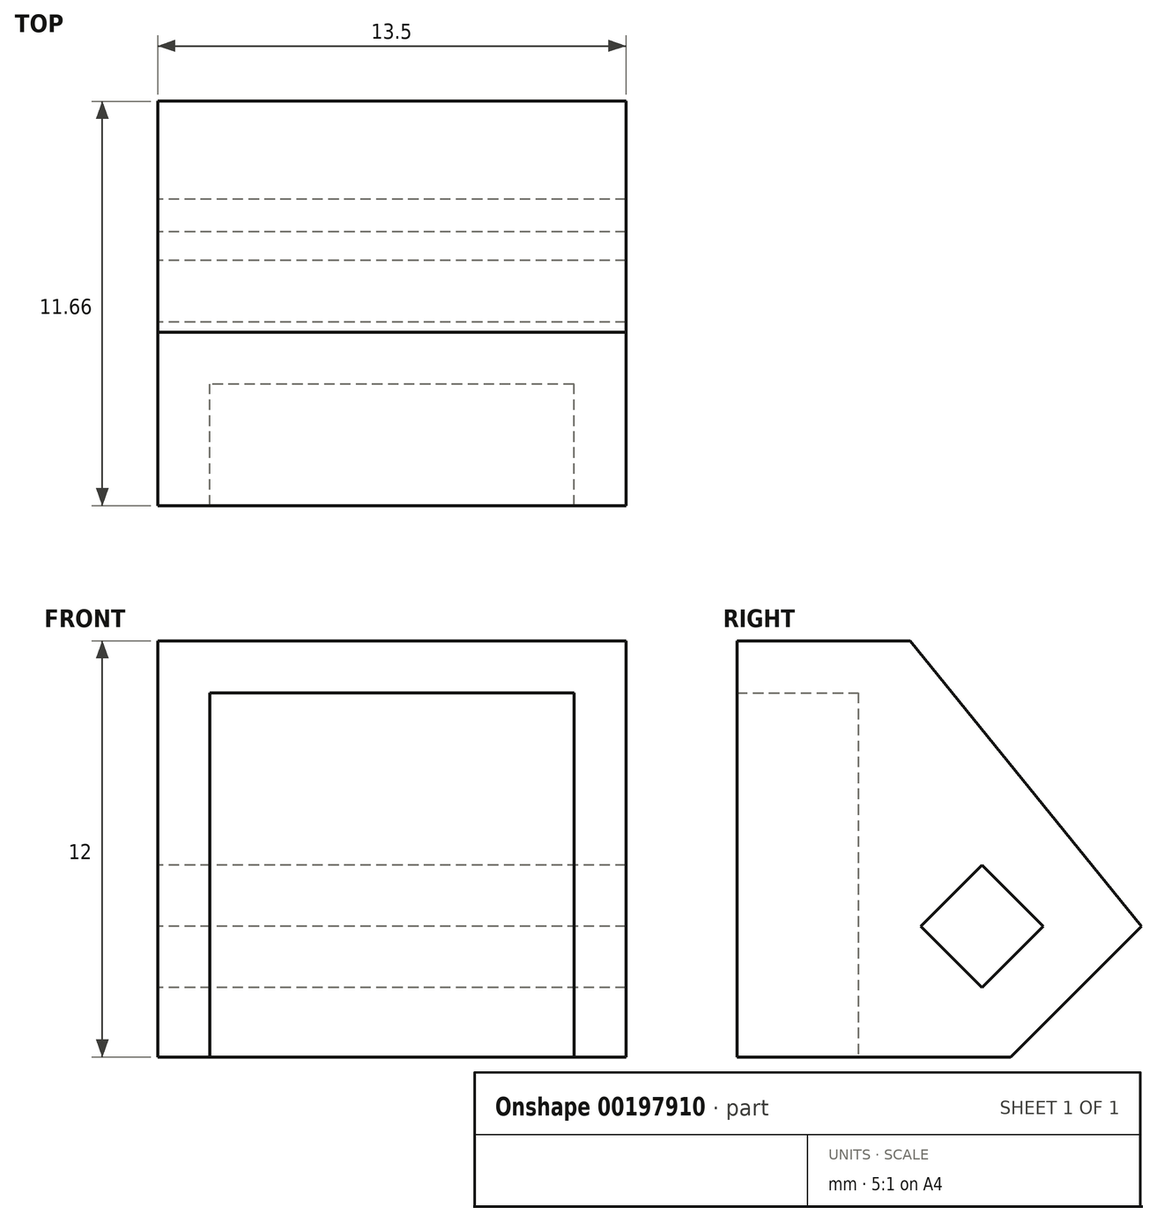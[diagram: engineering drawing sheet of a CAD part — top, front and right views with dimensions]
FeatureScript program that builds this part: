
annotation { "Feature Type Name" : "Feature", "Feature Type Description" : "" }
export const myFeature = defineFeature(function(context is Context, id is Id, definition is map)
    precondition{}
    {
        {
            var Q0;
            Q0=qCreatedBy(makeId("Front.planeOp"),FACE);
            var sketch = newSketch(context, id + "F0", { "sketchPlane" : qUnion([Q0])});
            skLineSegment(sketch, "E0.bottom", {"start": v(5.25, 5.25) * mm, "end": v(-5.25, 5.25) * mm});
            skLineSegment(sketch, "E0.top", {"start": v(5.25, -5.25) * mm, "end": v(-5.25, -5.25) * mm});
            skLineSegment(sketch, "E0.left", {"start": v(5.25, 5.25) * mm, "end": v(5.25, -5.25) * mm});
            skLineSegment(sketch, "E0.right", {"start": v(-5.25, 5.25) * mm, "end": v(-5.25, -5.25) * mm});
            skPoint(sketch, "E0.middle", {"position": v(0, 0) * mm});
            skLineSegment(sketch, "E1.0", {"start": v(7.25, -7.25) * mm, "end": v(-7.25, -7.25) * mm, "construction": true});
            skLineSegment(sketch, "E1.1", {"start": v(7.25, 7.25) * mm, "end": v(7.25, -7.25) * mm, "construction": true});
            skLineSegment(sketch, "E1.2", {"start": v(7.25, 7.25) * mm, "end": v(-7.25, 7.25) * mm, "construction": true});
            skLineSegment(sketch, "E1.3", {"start": v(-7.25, 7.25) * mm, "end": v(-7.25, -7.25) * mm, "construction": true});
            skSolve(sketch);
        }
        {
            var Q0;
            Q0=makeQuery(id+"F0.imprint","IMPRINT",FACE,{"disambiguationData":[TD([[makeQuery(id+"F0.imprint","IMPRINT",EDGE,{"derivedFrom":sQuery(id+"F0.wireOp",EDGE,"E0.bottom")}),1.0]])]});
            extrude(context, id + "F1", {"entities" : qUnion([Q0]), "depth" : 1.5 * mm});
        }
        {
            var Q0;
            Q0=makeQuery(id+"F1.opExtrude","CAP_FACE",FACE,{"disambiguationData":[OSD([sQuery(id+"F0.wireOp",EDGE,"E0.bottom"),sQuery(id+"F0.wireOp",EDGE,"E0.top"),sQuery(id+"F0.wireOp",EDGE,"E0.left"),sQuery(id+"F0.wireOp",EDGE,"E0.right")])],"isStart":true});
            var sketch = newSketch(context, id + "F2", { "sketchPlane" : qUnion([Q0])});
            skLineSegment(sketch, "E2", {"start": v(-5.25, -5.25) * mm, "end": v(-6.75, -5.25) * mm});
            skLineSegment(sketch, "E3", {"start": v(-6.75, -5.25) * mm, "end": v(-6.75, 6.75) * mm});
            skLineSegment(sketch, "E4", {"start": v(-6.75, 6.75) * mm, "end": v(6.75, 6.75) * mm});
            skLineSegment(sketch, "E5", {"start": v(6.75, 6.75) * mm, "end": v(6.75, -5.25) * mm});
            skLineSegment(sketch, "E6", {"start": v(6.75, -5.25) * mm, "end": v(5.25, -5.25) * mm});
            skLineSegment(sketch, "E7", {"start": v(5.25, -5.25) * mm, "end": v(5.25, 5.25) * mm});
            skLineSegment(sketch, "E8", {"start": v(5.25, 5.25) * mm, "end": v(-5.25, 5.25) * mm});
            skLineSegment(sketch, "E9", {"start": v(-5.25, 5.25) * mm, "end": v(-5.25, -5.25) * mm});
            skSolve(sketch);
        }
        {
            var Q0;
            Q0=makeQuery(id+"F2.imprint","IMPRINT",FACE,{"disambiguationData":[TD([[makeQuery(id+"F2.imprint","IMPRINT",EDGE,{"derivedFrom":sQuery(id+"F2.wireOp",EDGE,"E2")}),-1.0]])]});
            extrude(context, id + "F3", {"entities" : qUnion([Q0]), "operationType" : NewBodyOperationType.ADD, "oppositeDirection" : true, "depth" : 5 * mm});
        }
        {
            var Q0;
            Q0=qCreatedBy(makeId("Right.planeOp"),FACE);
            var sketch = newSketch(context, id + "F4", { "sketchPlane" : qUnion([Q0])});
            skCircle(sketch, "E10", {"center": v(2.06, -1.48) * mm, "radius": 1.25 * mm, "construction": true});
            skLineSegment(sketch, "E11", {"start": v(0, -5.25) * mm, "end": v(2.9, -5.25) * mm});
            skLineSegment(sketch, "E12", {"start": v(0, 6.75) * mm, "end": v(6.66, -1.48) * mm});
            skLineSegment(sketch, "E13", {"start": v(0, 6.75) * mm, "end": v(0, -5.25) * mm});
            skLineSegment(sketch, "E14.bottom", {"start": v(0.3, -1.48) * mm, "end": v(2.06, 0.29) * mm});
            skLineSegment(sketch, "E14.top", {"start": v(2.06, -3.25) * mm, "end": v(3.83, -1.48) * mm});
            skLineSegment(sketch, "E14.left", {"start": v(0.3, -1.48) * mm, "end": v(2.06, -3.25) * mm});
            skLineSegment(sketch, "E14.right", {"start": v(2.06, 0.29) * mm, "end": v(3.83, -1.48) * mm});
            skLineSegment(sketch, "E15", {"start": v(2.9, -5.25) * mm, "end": v(6.66, -1.48) * mm});
            skSolve(sketch);
        }
        {
            var Q0;
            {var subQ1=sQuery(id+"F4.wireOp",EDGE,"E11");Q0=makeQuery(id+"F4.imprint","IMPRINT",FACE,{"disambiguationData":[TD([[makeQuery(id+"F4.imprint","IMPRINT",EDGE,{"derivedFrom":subQ1}),1.0]])]});}
            var Q1;
            Q1=makeQuery(id+"F3.opExtrude","CAP_VERTEX",VERTEX,{"disambiguationData":[OSD([sQuery(id+"F2.wireOp",EDGE,"E2"),sQuery(id+"F2.wireOp",EDGE,"E3")])],"isStart":true});
            var Q2;
            Q2=makeQuery(id+"F3.opExtrude","SWEPT_FACE",FACE,{"disambiguationData":[OSD([sQuery(id+"F2.wireOp",EDGE,"E3")])]});
            var Q3;
            Q3=makeQuery(id+"F3.opExtrude","CAP_VERTEX",VERTEX,{"disambiguationData":[OSD([sQuery(id+"F2.wireOp",EDGE,"E5"),sQuery(id+"F2.wireOp",EDGE,"E6")])],"isStart":true});
            extrude(context, id + "F5", {"entities" : qUnion([Q0]), "operationType" : NewBodyOperationType.ADD, "endBound" : BoundingType.UP_TO_VERTEX, "endBoundEntityVertex" : qUnion([Q1]), "depth" : 11.56 * mm, "hasSecondDirection" : true, "secondDirectionBound" : SecondDirectionBoundingType.UP_TO_VERTEX, "secondDirectionOppositeDirection" : true, "secondDirectionBoundEntityFace" : qUnion([Q2]), "secondDirectionBoundEntityVertex" : qUnion([Q3]), "secondDirectionDepth" : 25 * mm});
        }
    });
